# Revit family: HL_Сифон с уплотнением_HL138
name_source: partatom
category: Příslušenství trubek
revit_build: Autodesk Revit 2016 (Build: 20161004_0715(x64)
units: mm (PartAtom-declared; Revit-internal decimal feet)

## family parameters
Kóta kulaté spojky = Použít průměr
Nadpis OmniClass = General Pipework and Ductwork Products
Ořezat dutým tvarem při načtení = Ne
Sdílené = Ne
Typ součásti = Normální
Vždy vertikální = Ano
Založené na pracovní rovině = Ne
Číslo OmniClass = 23.60.30.00

## types (1)
- HL_Сифон с уплотнением_HL138
    Cena = 0 $
    EAN = 9003076030705
    Komentáře k typům = Встроенный сифон DN32 для сброса дренажа от кондиционеров
    Model = HL138
    Popis = Кондиционирование и Вентиляция
    URL = http://www.hutterer-lechner.com
    Výrobce = HL Hutterer & Lechner GmbH
    ВЕС = 0,28 kg
    ВЫСОТА МОНТАЖА = 60 - 110 mm
    МАТЕРИАЛ = PP
    НОМИНАЛЬНЫЙ ДИАМЕТР 2 = 32 mm
    ПРИЁМНОЕ ОТВЕРСТИЕ = Ø 20 - 32 mm
    ПРОИЗВОДИТЕЛЬНОСТЬ = 0,15 l/s
    ПРОПУСКНАЯ СПОСОБНОСТЬ = 0.0 m³/h
    РАЗМЕР = DN32
    материал = Plactic - White
    материал 2 = Plactic - Black
    материал 3 = Plastic - Red
